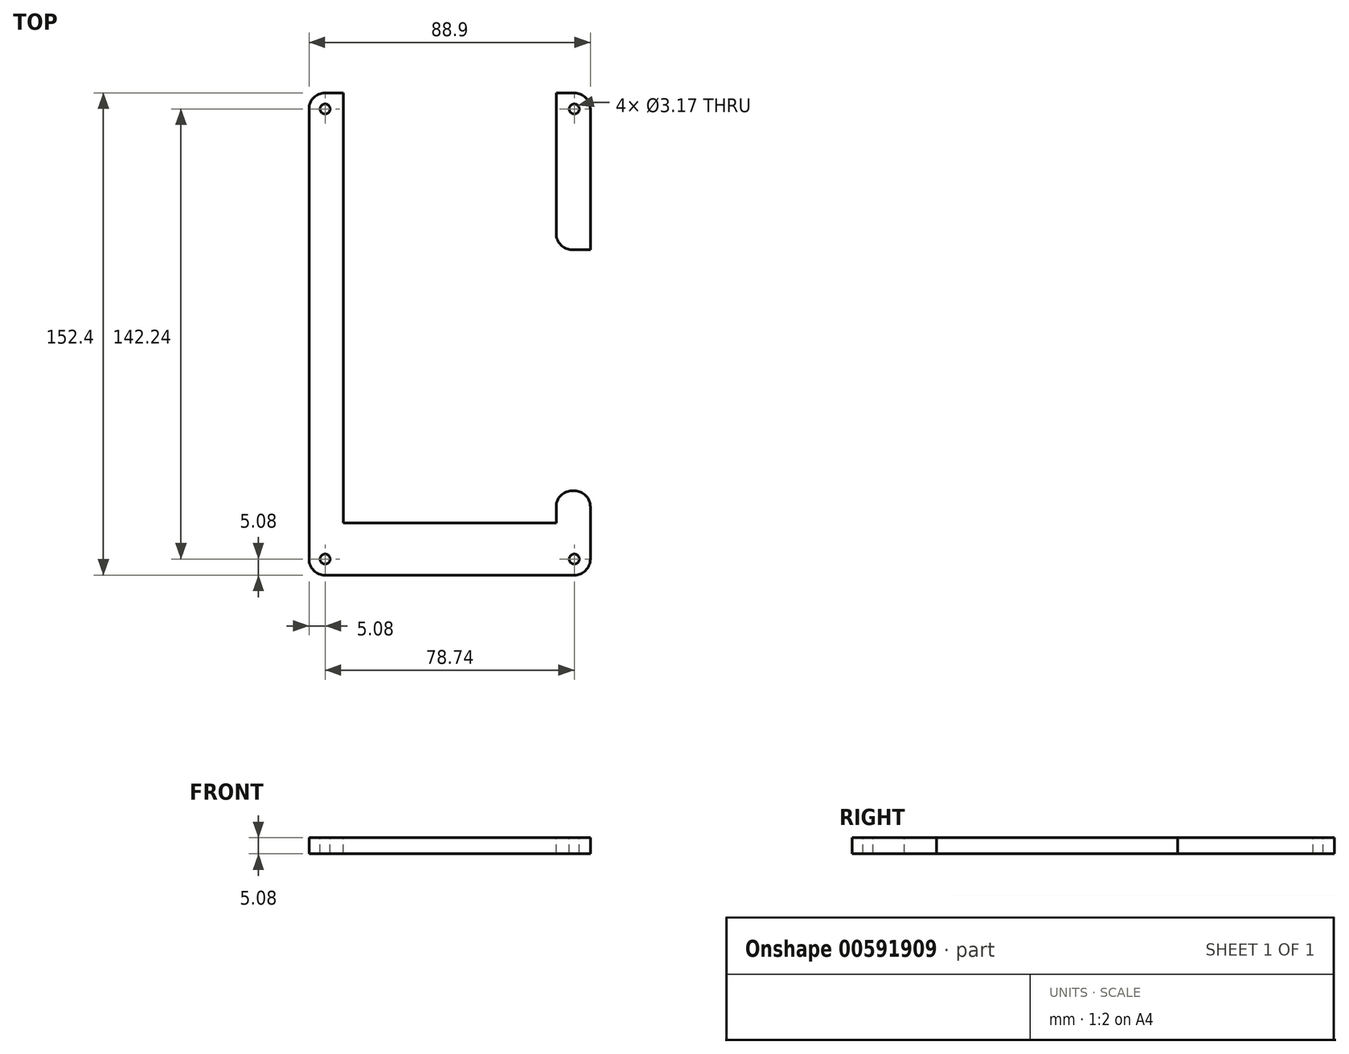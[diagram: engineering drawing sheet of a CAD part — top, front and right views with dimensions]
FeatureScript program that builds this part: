
annotation { "Feature Type Name" : "Feature", "Feature Type Description" : "" }
export const myFeature = defineFeature(function(context is Context, id is Id, definition is map)
    precondition{}
    {
        {
            var Q0;
            Q0=qCreatedBy(makeId("Top.planeOp"),FACE);
            var sketch = newSketch(context, id + "F0", { "sketchPlane" : qUnion([Q0])});
            skLineSegment(sketch, "E0.bottom", {"start": v(0, 0) * mm, "end": v(88.9, 0) * mm});
            skLineSegment(sketch, "E0.top", {"start": v(0, -152.4) * mm, "end": v(88.9, -152.4) * mm});
            skLineSegment(sketch, "E0.left", {"start": v(0, 0) * mm, "end": v(0, -152.4) * mm});
            skLineSegment(sketch, "E0.right", {"start": v(88.9, 0) * mm, "end": v(88.9, -152.4) * mm});
            skSolve(sketch);
        }
        {
            var Q0;
            Q0=makeQuery(id+"F0.imprint","IMPRINT",FACE,{"disambiguationData":[TD([[makeQuery(id+"F0.imprint","IMPRINT",EDGE,{"derivedFrom":sQuery(id+"F0.wireOp",EDGE,"E0.bottom")}),-1.0]])]});
            extrude(context, id + "F1", {"entities" : qUnion([Q0]), "depth" : 5.08 * mm, "offsetDistance" : 25.4 * mm});
        }
        {
            var Q0;
            Q0=makeQuery(id+"F1.opExtrude","CAP_FACE",FACE,{"disambiguationData":[OSD([sQuery(id+"F0.wireOp",EDGE,"E0.bottom"),sQuery(id+"F0.wireOp",EDGE,"E0.top"),sQuery(id+"F0.wireOp",EDGE,"E0.left"),sQuery(id+"F0.wireOp",EDGE,"E0.right")])],"isStart":false});
            var sketch = newSketch(context, id + "F2", { "sketchPlane" : qUnion([Q0])});
            skLineSegment(sketch, "E1.bottom", {"start": v(10.8, 0) * mm, "end": v(78.1, 0) * mm});
            skLineSegment(sketch, "E1.top", {"start": v(10.8, -135.9) * mm, "end": v(78.1, -135.9) * mm});
            skLineSegment(sketch, "E1.left", {"start": v(10.8, 0) * mm, "end": v(10.8, -135.9) * mm});
            skLineSegment(sketch, "E1.right", {"start": v(78.1, 0) * mm, "end": v(78.1, -49.53) * mm});
            skLineSegment(sketch, "E2", {"start": v(78.1, -49.53) * mm, "end": v(88.9, -49.53) * mm});
            skLineSegment(sketch, "E3", {"start": v(78.1, -125.73) * mm, "end": v(88.9, -125.73) * mm});
            skLineSegment(sketch, "E4.trimOffspring", {"start": v(78.1, -125.73) * mm, "end": v(78.1, -135.9) * mm});
            skSolve(sketch);
        }
        {
            var Q0;
            Q0=makeQuery(id+"F2.imprint","IMPRINT",FACE,{"disambiguationData":[TD([[makeQuery(id+"F2.imprint","IMPRINT",EDGE,{"derivedFrom":sQuery(id+"F2.wireOp",EDGE,"E1.bottom")}),-1.0]])]});
            extrude(context, id + "F3", {"entities" : qUnion([Q0]), "operationType" : NewBodyOperationType.REMOVE, "oppositeDirection" : true, "depth" : 25.4 * mm, "offsetDistance" : 25.4 * mm});
        }
        {
            var Q0;
            {var subQ0=sQuery(id+"F0.wireOp",EDGE,"E0.left");var subQ1=sQuery(id+"F0.wireOp",EDGE,"E0.top");var subQ2=sQuery(id+"F0.wireOp",EDGE,"E0.right");var subQ3=sQuery(id+"F0.wireOp",EDGE,"E0.bottom");Q0=makeQuery(id+"F3.boolean.opBoolean","SPLIT",FACE,{"disambiguationData":[TD([makeQuery(id+"F1.opExtrude","SWEPT_FACE",FACE,{"disambiguationData":[OSD([subQ1])]})])],"derivedFrom":makeQuery(id+"F1.opExtrude","CAP_FACE",FACE,{"disambiguationData":[OSD([subQ3,subQ1,subQ0,subQ2])],"isStart":false})});}
            var sketch = newSketch(context, id + "F4", { "sketchPlane" : qUnion([Q0])});
            skCircle(sketch, "E5", {"center": v(5.08, -5.08) * mm, "radius": 1.59 * mm});
            skCircle(sketch, "E6", {"center": v(83.82, -147.32) * mm, "radius": 1.59 * mm});
            skCircle(sketch, "E7", {"center": v(5.08, -147.32) * mm, "radius": 1.59 * mm});
            skCircle(sketch, "E8", {"center": v(83.82, -5.08) * mm, "radius": 1.59 * mm});
            skSolve(sketch);
        }
        {
            var Q0;
            Q0=makeQuery(id+"F4.imprint","IMPRINT",FACE,{"disambiguationData":[TD([[makeQuery(id+"F4.imprint","IMPRINT",EDGE,{"derivedFrom":sQuery(id+"F4.wireOp",EDGE,"E7")}),1.0]])]});
            var Q1;
            Q1=makeQuery(id+"F4.imprint","IMPRINT",FACE,{"disambiguationData":[TD([[makeQuery(id+"F4.imprint","IMPRINT",EDGE,{"derivedFrom":sQuery(id+"F4.wireOp",EDGE,"E6")}),1.0]])]});
            var Q2;
            Q2=makeQuery(id+"F4.imprint","IMPRINT",FACE,{"disambiguationData":[TD([[makeQuery(id+"F4.imprint","IMPRINT",EDGE,{"derivedFrom":sQuery(id+"F4.wireOp",EDGE,"E8")}),1.0]])]});
            var Q3;
            Q3=makeQuery(id+"F4.imprint","IMPRINT",FACE,{"disambiguationData":[TD([[makeQuery(id+"F4.imprint","IMPRINT",EDGE,{"derivedFrom":sQuery(id+"F4.wireOp",EDGE,"E5")}),1.0]])]});
            extrude(context, id + "F5", {"entities" : qUnion([Q0, Q1, Q2, Q3]), "operationType" : NewBodyOperationType.REMOVE, "oppositeDirection" : true, "depth" : 25.4 * mm, "offsetDistance" : 25.4 * mm});
        }
        {
            var Q0;
            Q0=makeQuery(id+"F1.opExtrude","SWEPT_EDGE",EDGE,{"disambiguationData":[OSD([sQuery(id+"F0.wireOp",EDGE,"E0.top"),sQuery(id+"F0.wireOp",EDGE,"E0.left")])]});
            var Q1;
            Q1=makeQuery(id+"F1.opExtrude","SWEPT_EDGE",EDGE,{"disambiguationData":[OSD([sQuery(id+"F0.wireOp",EDGE,"E0.top"),sQuery(id+"F0.wireOp",EDGE,"E0.right")])]});
            var Q2;
            Q2=makeQuery(id+"F1.opExtrude","SWEPT_EDGE",EDGE,{"disambiguationData":[OSD([sQuery(id+"F0.wireOp",EDGE,"E0.bottom"),sQuery(id+"F0.wireOp",EDGE,"E0.left")])]});
            var Q3;
            Q3=makeQuery(id+"F1.opExtrude","SWEPT_EDGE",EDGE,{"disambiguationData":[OSD([sQuery(id+"F0.wireOp",EDGE,"E0.bottom"),sQuery(id+"F0.wireOp",EDGE,"E0.right")])]});
            var Q4;
            Q4=makeQuery(id+"F3.boolean.opBoolean","COPY",EDGE,{"derivedFrom":makeQuery(id+"F3.opExtrude","SWEPT_EDGE",EDGE,{"disambiguationData":[OSD([sQuery(id+"F2.wireOp",EDGE,"E1.right"),sQuery(id+"F2.wireOp",EDGE,"E2")])]})});
            var Q5;
            Q5=makeQuery(id+"F3.boolean.opBoolean","COPY",EDGE,{"derivedFrom":makeQuery(id+"F3.opExtrude","SWEPT_EDGE",EDGE,{"disambiguationData":[OSD([sQuery(id+"F0.wireOp",EDGE,"E0.right"),sQuery(id+"F2.wireOp",EDGE,"E2")])]})});
            var Q6;
            Q6=makeQuery(id+"F3.boolean.opBoolean","COPY",EDGE,{"derivedFrom":makeQuery(id+"F3.opExtrude","SWEPT_EDGE",EDGE,{"disambiguationData":[OSD([sQuery(id+"F0.wireOp",EDGE,"E0.right"),sQuery(id+"F2.wireOp",EDGE,"E3")])]})});
            var Q7;
            Q7=makeQuery(id+"F3.boolean.opBoolean","COPY",EDGE,{"derivedFrom":makeQuery(id+"F3.opExtrude","SWEPT_EDGE",EDGE,{"disambiguationData":[OSD([sQuery(id+"F2.wireOp",EDGE,"E3"),sQuery(id+"F2.wireOp",EDGE,"E4.trimOffspring")])]})});
            fillet(context, id + "F6", {"entities" : qUnion([Q0, Q1, Q2, Q3, Q4, Q5, Q6, Q7]), "tangentPropagation" : true, "radius" : 5.08 * mm, "defaultsChanged" : false, "vertexSettings" : [], "allowEdgeOverflow" : false});
        }
    });
